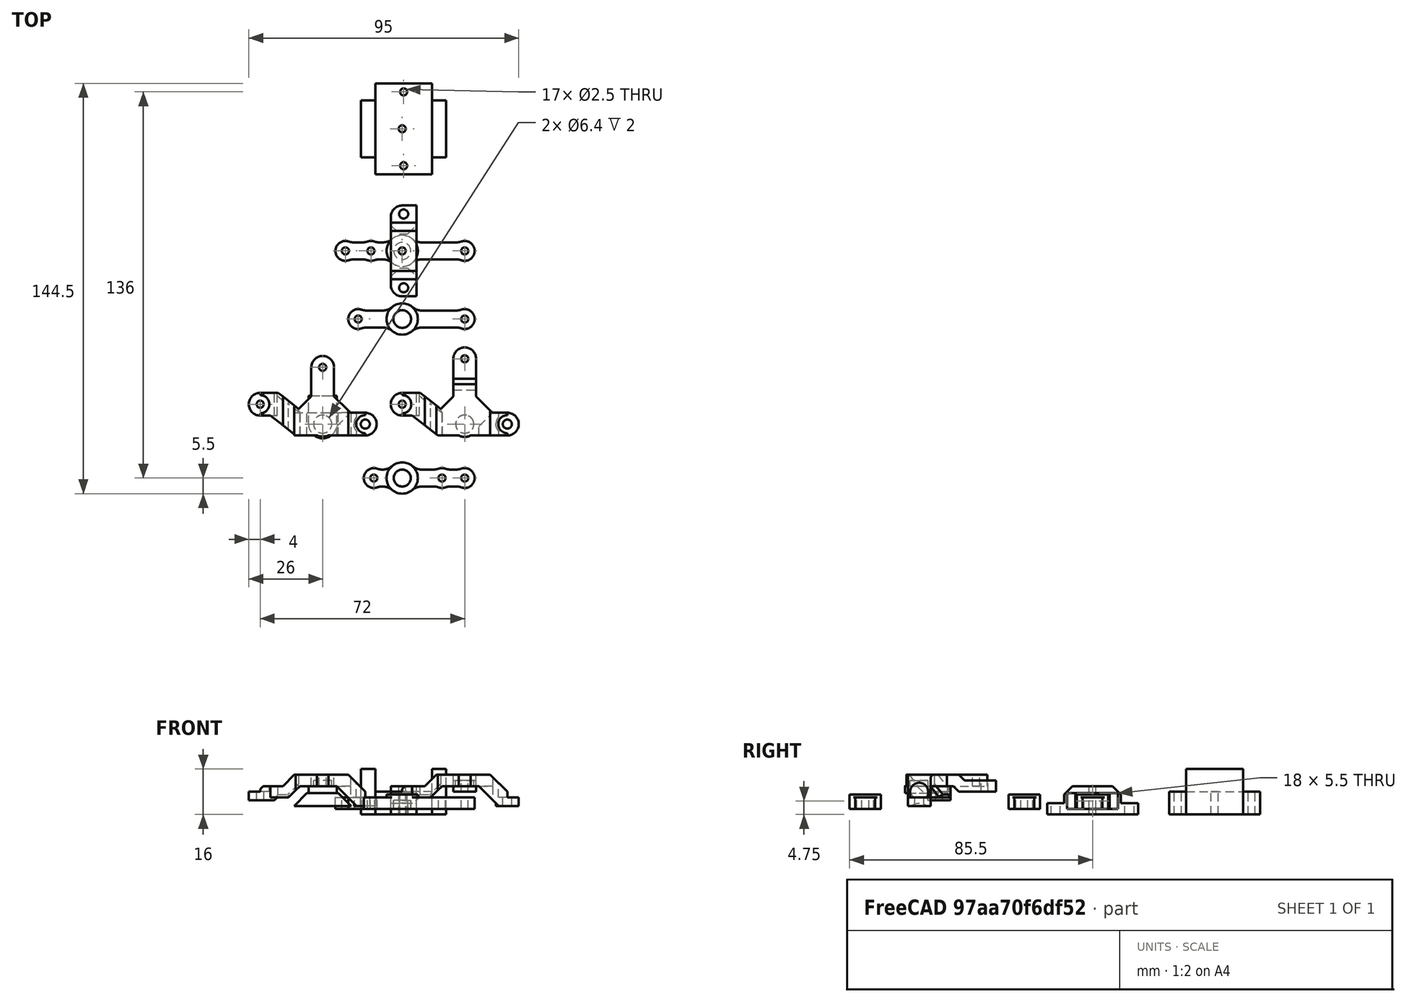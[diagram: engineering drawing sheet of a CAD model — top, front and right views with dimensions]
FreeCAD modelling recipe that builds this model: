
FCSTD DOCUMENT  (FreeCAD 0.20R)
Label: steering-arms-04
License: CC-BY 3.0
LicenseURL: http://creativecommons.org/licenses/by/3.0/
objects: Part::Cylinder×49, Part::MultiFuse×31, Part::Box×30, Part::Cut×30, Part::Chamfer×13, Part::Fillet×5, App::DocumentObjectGroup×2, Part::Mirroring×1
note: 159 computed .brp shape members not serialized (recipe doc carries the construction recipe); baked Part::Feature solids carry a one-line shape summary decoded from their .brp

FEATURE [Part::Cylinder] Cylinder011
  Angle = 360
  AttacherType = Attacher::AttachEngine3D
  FirstAngle = 0
  Height = 2.5
  Placement = pos=(-15,0,5.5) rot=(0,0,1;0rad)
  Radius = 5
  SecondAngle = 0
FEATURE [Part::Box] Box014  label="Cube014"
  AttacherType = Attacher::AttachEngine3D
  Height = 2.5
  Length = 10
  Placement = pos=(-20,0,5.5) rot=(0,0,1;0rad)
  Width = 10
FEATURE [Part::MultiFuse] Fusion006
  Refine = true
  Shapes = -> [Cylinder011,Box014]
FEATURE [Part::Box] Box015  label="Cube015"
  AttacherType = Attacher::AttachEngine3D
  Height = 4.5
  Length = 20
  Placement = pos=(-25,-4,1) rot=(0,0,1;0rad)
  Width = 8
FEATURE [Part::Chamfer] Chamfer001
  Base = -> Box015
  Edges = 2 edges r=4.49: [Edge2,Edge6]
FEATURE [Part::MultiFuse] Fusion008  label="axle"
  Refine = true
  Shapes = -> [Chamfer001,Fusion006]
FEATURE [Part::Cylinder] Cylinder016
  Angle = 360
  AttacherType = Attacher::AttachEngine3D
  FirstAngle = 0
  Height = 3
  Placement = pos=(0,0,1) rot=(0,0,1;0rad)
  Radius = 4
  SecondAngle = 0
FEATURE [Part::Cylinder] Cylinder017
  Angle = 360
  AttacherType = Attacher::AttachEngine3D
  FirstAngle = 0
  Height = 3
  Placement = pos=(-37,7,3) rot=(0,0,1;0rad)
  Radius = 4
  SecondAngle = 0
FEATURE [Part::Cylinder] Cylinder018
  Angle = 360
  AttacherType = Attacher::AttachEngine3D
  FirstAngle = 0
  Height = 4
  Placement = pos=(-15,0,8) rot=(0,0,1;0rad)
  Radius = 4.5
  SecondAngle = 0
FEATURE [Part::Box] Box021  label="Cube021"
  AttacherType = Attacher::AttachEngine3D
  Height = 4
  Length = 8
  Placement = pos=(-19,0,8) rot=(0,0,1;0rad)
  Width = 27
FEATURE [Part::Cylinder] Cylinder019
  Angle = 360
  AttacherType = Attacher::AttachEngine3D
  FirstAngle = 0
  Height = 4
  Placement = pos=(-15,27,8) rot=(0,0,1;0rad)
  Radius = 4
  SecondAngle = 0
FEATURE [Part::Cylinder] Cylinder020
  Angle = 360
  AttacherType = Attacher::AttachEngine3D
  FirstAngle = 0
  Height = 2
  Placement = pos=(-15,0,8) rot=(0,0,1;0rad)
  Radius = 3.2
  SecondAngle = 0
FEATURE [Part::Box] Box022  label="Cube022"
  AttacherType = Attacher::AttachEngine3D
  Height = 4
  Length = 11
  Placement = pos=(-15,-4,8) rot=(0,0,1;0rad)
  Width = 8
FEATURE [Part::Box] Box023  label="Cube023"
  AttacherType = Attacher::AttachEngine3D
  Height = 4
  Length = 6
  Placement = pos=(-37,3,8) rot=(0,0,1;0rad)
  Width = 8
FEATURE [Part::Box] Box024  label="Cube024"
  AttacherType = Attacher::AttachEngine3D
  Height = 4
  Length = 15
  Placement = pos=(-36,5,8) rot=(0,0,-1;0.663225rad)
  Width = 8
FEATURE [Part::Box] Box025  label="Cube025"
  AttacherType = Attacher::AttachEngine3D
  Height = 4
  Length = 9
  Placement = pos=(-24,-4,8) rot=(0,0,1;0rad)
  Width = 8
FEATURE [Part::Box] Box026  label="Cube026"
  AttacherType = Attacher::AttachEngine3D
  Height = 4
  Length = 10
  Placement = pos=(-30,-14,8) rot=(0,0,1;0rad)
  Width = 10
FEATURE [Part::Box] Box027  label="Cube027"
  AttacherType = Attacher::AttachEngine3D
  Height = 4
  Length = 10
  Placement = pos=(-35,11,8) rot=(0,0,1;0rad)
  Width = 10
FEATURE [Part::MultiFuse] Fusion016
  Refine = true
  Shapes = -> [Box026,Box027]
FEATURE [Part::MultiFuse] Fusion017
  Refine = true
  Shapes = -> [Box023,Box024,Box025]
FEATURE [Part::Cut] Cut012
  Base = -> Fusion017
  Refine = true
  Tool = -> Fusion016
FEATURE [Part::Cylinder] Cylinder021
  Angle = 360
  AttacherType = Attacher::AttachEngine3D
  FirstAngle = 0
  Height = 10
  Radius = 1.6
  SecondAngle = 0
FEATURE [Part::Cylinder] Cylinder022
  Angle = 360
  AttacherType = Attacher::AttachEngine3D
  FirstAngle = 0
  Height = 10
  Placement = pos=(-37,7,2) rot=(0,0,1;0rad)
  Radius = 1.6
  SecondAngle = 0
FEATURE [Part::Box] Box028  label="Cube028"
  AttacherType = Attacher::AttachEngine3D
  Height = 4
  Length = 14
  Placement = pos=(-15,-6,8) rot=(0,0,1;0.785398rad)
  Width = 14
FEATURE [Part::Box] Box029  label="Cube029"
  AttacherType = Attacher::AttachEngine3D
  Height = 4
  Length = 10
  Placement = pos=(-20,-14,8) rot=(0,0,1;0rad)
  Width = 10
FEATURE [Part::Cut] Cut013
  Base = -> Box028
  Refine = true
  Tool = -> Box029
FEATURE [Part::MultiFuse] Fusion018
  Refine = true
  Shapes = -> [Box022,Box021,Cut013,Cut012,Cylinder019,Cylinder018]
FEATURE [Part::Cut] Cut014
  Base = -> Fusion018
  Refine = true
  Tool = -> Cylinder020
FEATURE [Part::Box] Box032  label="Cube032"
  AttacherType = Attacher::AttachEngine3D
  Height = 11
  Length = 10
  Placement = pos=(-10,-4,1) rot=(0,0,1;0rad)
  Width = 8
FEATURE [Part::Chamfer] Chamfer012
  Base = -> Box032
  Edges = 1 edges r=7: [Edge4]
FEATURE [Part::Chamfer] Chamfer013
  Base = -> Chamfer012
  Edges = 1 edges r=6: [Edge12]
FEATURE [Part::Chamfer] Chamfer014
  Base = -> Cut014
  Edges = 1 edges r=2: [Edge2]
FEATURE [Part::MultiFuse] Fusion020
  Refine = true
  Shapes = -> [Chamfer014,Chamfer013]
FEATURE [Part::Cylinder] Cylinder024
  Angle = 360
  AttacherType = Attacher::AttachEngine3D
  FirstAngle = 0
  Height = 10
  Placement = pos=(0,0,4) rot=(0,0,1;0rad)
  Radius = 3.2
  SecondAngle = 0
FEATURE [Part::Cut] Cut015
  Base = -> Fusion020
  Refine = true
  Tool = -> Cylinder024
FEATURE [Part::Box] Box033  label="Cube033"
  AttacherType = Attacher::AttachEngine3D
  Height = 8
  Length = 10
  Placement = pos=(-10.2,-1,0) rot=(0,0,1;0.785398rad)
  Width = 10
FEATURE [Part::Cut] Cut016
  Base = -> Cut015
  Refine = true
  Tool = -> Box033
FEATURE [Part::MultiFuse] Fusion022
  Refine = true
  Shapes = -> [Cylinder016,Cut016]
FEATURE [Part::Cylinder] Cylinder025
  Angle = 360
  AttacherType = Attacher::AttachEngine3D
  FirstAngle = 0
  Height = 10
  Placement = pos=(-15,27,4) rot=(0,0,1;0rad)
  Radius = 1.6
  SecondAngle = 0
FEATURE [Part::MultiFuse] Fusion023
  Refine = true
  Shapes = -> [Cylinder021,Cylinder025]
FEATURE [Part::Cut] Cut017
  Base = -> Fusion022
  Refine = true
  Tool = -> Fusion023
FEATURE [Part::MultiFuse] Fusion024
  Refine = true
  Shapes = -> [Box026,Box027]
FEATURE [Part::MultiFuse] Fusion025
  Refine = true
  Shapes = -> [Box023,Box024,Box025]
FEATURE [Part::Cut] Cut018
  Base = -> Fusion025
  Placement = pos=(0,0,-4) rot=(0,0,1;0rad)
  Refine = true
  Tool = -> Fusion024
FEATURE [Part::Box] Box034  label="Cube034"
  AttacherType = Attacher::AttachEngine3D
  Height = 10
  Length = 10
  Placement = pos=(-23,-4,0) rot=(0,0,1;0rad)
  Width = 11
FEATURE [Part::Cut] Cut019
  Base = -> Cut018
  Refine = true
  Tool = -> Box034
FEATURE [Part::Chamfer] Chamfer015
  Base = -> Cut019
  Edges = 1 edges r=3.99: [Edge20]
FEATURE [Part::Box] Box035  label="Cube035"
  AttacherType = Attacher::AttachEngine3D
  Height = 10
  Length = 10
  Placement = pos=(-39,-2,8) rot=(0,0,1;0rad)
  Width = 15
FEATURE [Part::Cut] Cut020
  Base = -> Cut017
  Refine = true
  Tool = -> Box035
FEATURE [Part::Chamfer] Chamfer016
  Base = -> Cut020
  Edges = 1 edges r=3.99: [Edge32]
FEATURE [Part::MultiFuse] Fusion026
  Refine = true
  Shapes = -> [Chamfer015,Chamfer016]
FEATURE [Part::MultiFuse] Fusion027
  Refine = true
  Shapes = -> [Cylinder017,Fusion026]
FEATURE [Part::Cylinder] Cylinder026
  Angle = 360
  AttacherType = Attacher::AttachEngine3D
  FirstAngle = 0
  Height = 10
  Placement = pos=(-37,7,6) rot=(0,0,1;0rad)
  Radius = 3.2
  SecondAngle = 0
FEATURE [Part::Chamfer] Chamfer017
  Base = -> Fusion027
  Edges = 1 edges r=1: [Edge20]
FEATURE [Part::Cut] Cut021
  Base = -> Chamfer017
  Refine = true
  Tool = -> Cylinder026
FEATURE [Part::Box] Box036  label="Cube036"
  AttacherType = Attacher::AttachEngine3D
  Height = 1
  Length = 6
  Placement = pos=(-37,3,3) rot=(0,0,1;0rad)
  Width = 8
FEATURE [Part::MultiFuse] Fusion028
  Refine = true
  Shapes = -> [Cut021,Box036]
FEATURE [Part::Chamfer] Chamfer018
  Base = -> Fusion028
  Edges = 1 edges r=0.99: [Edge51]
FEATURE [Part::Cut] Cut022
  Base = -> Chamfer018
  Refine = true
  Tool = -> Cylinder022
FEATURE [Part::Chamfer] Chamfer019
  Base = -> Cut022
  Edges = 2 edges r=1: [Edge17,Edge50]
FEATURE [Part::Box] Box037  label="Cube037"
  AttacherType = Attacher::AttachEngine3D
  Height = 10
  Length = 10
  Placement = pos=(-19,23,3) rot=(0,0,1;0rad)
  Width = 10
FEATURE [Part::Cut] Cut023
  Base = -> Chamfer019
  Refine = true
  Tool = -> Box037
FEATURE [Part::Cylinder] Cylinder027
  Angle = 360
  AttacherType = Attacher::AttachEngine3D
  FirstAngle = 0
  Height = 4
  Placement = pos=(-15,23,8) rot=(0,0,1;0rad)
  Radius = 4
  SecondAngle = 0
FEATURE [Part::MultiFuse] Fusion029
  Refine = true
  Shapes = -> [Cut023,Cylinder027]
FEATURE [Part::Cylinder] Cylinder028
  Angle = 360
  AttacherType = Attacher::AttachEngine3D
  FirstAngle = 0
  Height = 4
  Placement = pos=(-15,23,8) rot=(0,0,1;0rad)
  Radius = 1.6
  SecondAngle = 0
FEATURE [Part::Cut] Cut024
  Base = -> Fusion029
  Placement = pos=(50,0,0) rot=(0,0,1;0rad)
  Refine = true
  Tool = -> Cylinder028
FEATURE [Part::Cylinder] Cylinder029
  Angle = 360
  AttacherType = Attacher::AttachEngine3D
  FirstAngle = 0
  Height = 5
  Placement = pos=(13,0,0) rot=(0,0,1;0rad)
  Radius = 5.5
  SecondAngle = 0
FEATURE [Part::Cylinder] Cylinder030
  Angle = 360
  AttacherType = Attacher::AttachEngine3D
  FirstAngle = 0
  Height = 4
  Placement = pos=(35,0,0) rot=(0,0,1;0rad)
  Radius = 3.5
  SecondAngle = 0
FEATURE [Part::Box] Box038
  AttacherType = Attacher::AttachEngine3D
  Height = 4
  Length = 33
  Placement = pos=(2,-3,0) rot=(0,0,1;0rad)
  Width = 6
FEATURE [Part::Cylinder] Cylinder031
  Angle = 360
  AttacherType = Attacher::AttachEngine3D
  FirstAngle = 0
  Height = 4
  Placement = pos=(2,0,0) rot=(0,0,1;0rad)
  Radius = 3.5
  SecondAngle = 0
FEATURE [Part::MultiFuse] Fusion030
  Refine = true
  Shapes = -> [Cylinder029,Box038,Cylinder031,Cylinder030]
FEATURE [Part::Cylinder] Cylinder032
  Angle = 360
  AttacherType = Attacher::AttachEngine3D
  FirstAngle = 0
  Height = 5
  Placement = pos=(13,0,0) rot=(0,0,1;0rad)
  Radius = 3
  SecondAngle = 0
FEATURE [Part::Cylinder] Cylinder033
  Angle = 360
  AttacherType = Attacher::AttachEngine3D
  FirstAngle = 0
  Height = 4
  Placement = pos=(2,0,0) rot=(0,0,1;0rad)
  Radius = 1.25
  SecondAngle = 0
FEATURE [Part::Cylinder] Cylinder034
  Angle = 360
  AttacherType = Attacher::AttachEngine3D
  FirstAngle = 0
  Height = 4
  Placement = pos=(35,0,0) rot=(0,0,1;0rad)
  Radius = 1.25
  SecondAngle = 0
FEATURE [Part::MultiFuse] Fusion031
  Refine = true
  Shapes = -> [Cylinder032,Cylinder033,Cylinder034]
FEATURE [Part::Cut] Cut025
  Base = -> Fusion030
  Refine = true
  Tool = -> Fusion031
FEATURE [Part::Cylinder] Cylinder035
  Angle = 360
  AttacherType = Attacher::AttachEngine3D
  FirstAngle = 0
  Height = 5
  Placement = pos=(13,0,0) rot=(0,0,1;0rad)
  Radius = 5.5
  SecondAngle = 0
FEATURE [Part::Cylinder] Cylinder036
  Angle = 360
  AttacherType = Attacher::AttachEngine3D
  FirstAngle = 0
  Height = 4
  Placement = pos=(35,0,0) rot=(0,0,1;0rad)
  Radius = 3.5
  SecondAngle = 0
FEATURE [Part::Box] Box039
  AttacherType = Attacher::AttachEngine3D
  Height = 4
  Length = 38
  Placement = pos=(-3,-3,0) rot=(0,0,1;0rad)
  Width = 6
FEATURE [Part::Cylinder] Cylinder037
  Angle = 360
  AttacherType = Attacher::AttachEngine3D
  FirstAngle = 0
  Height = 4
  Placement = pos=(-2.5,0,0) rot=(0,0,1;0rad)
  Radius = 3.5
  SecondAngle = 0
FEATURE [Part::MultiFuse] Fusion032
  Refine = true
  Shapes = -> [Cylinder035,Box039,Cylinder037,Cylinder036]
FEATURE [Part::Cylinder] Cylinder038
  Angle = 360
  AttacherType = Attacher::AttachEngine3D
  FirstAngle = 0
  Height = 5
  Placement = pos=(13,0,0) rot=(0,0,1;0rad)
  Radius = 3.1
  SecondAngle = 0
FEATURE [Part::Cylinder] Cylinder039
  Angle = 360
  AttacherType = Attacher::AttachEngine3D
  FirstAngle = 0
  Height = 4
  Placement = pos=(-2.5,0,0) rot=(0,0,1;0rad)
  Radius = 1.25
  SecondAngle = 0
FEATURE [Part::Cylinder] Cylinder040
  Angle = 360
  AttacherType = Attacher::AttachEngine3D
  FirstAngle = 0
  Height = 4
  Placement = pos=(35,0,0) rot=(0,0,1;0rad)
  Radius = 1.25
  SecondAngle = 0
FEATURE [Part::MultiFuse] Fusion033
  Refine = true
  Shapes = -> [Cylinder038,Cylinder039,Cylinder040]
FEATURE [Part::Cut] Cut026
  Base = -> Fusion032
  Placement = pos=(0,25,0) rot=(0,0,1;0rad)
  Refine = true
  Tool = -> Fusion033
FEATURE [Part::Cylinder] Cylinder041
  Angle = 360
  AttacherType = Attacher::AttachEngine3D
  FirstAngle = 0
  Height = 4
  Placement = pos=(-7,0,0) rot=(0,0,1;0rad)
  Radius = 3.5
  SecondAngle = 0
FEATURE [Part::Cylinder] Cylinder042
  Angle = 360
  AttacherType = Attacher::AttachEngine3D
  FirstAngle = 0
  Height = 4
  Placement = pos=(-7,0,0) rot=(0,0,1;0rad)
  Radius = 1.25
  SecondAngle = 0
FEATURE [Part::Cylinder] Cylinder043
  Angle = 360
  AttacherType = Attacher::AttachEngine3D
  FirstAngle = 0
  Height = 5
  Placement = pos=(13,0,0) rot=(0,0,1;0rad)
  Radius = 5.5
  SecondAngle = 0
FEATURE [Part::Cylinder] Cylinder044
  Angle = 360
  AttacherType = Attacher::AttachEngine3D
  FirstAngle = 0
  Height = 4
  Placement = pos=(35,0,0) rot=(0,0,1;0rad)
  Radius = 3.5
  SecondAngle = 0
FEATURE [Part::Box] Box040
  AttacherType = Attacher::AttachEngine3D
  Height = 4
  Length = 32
  Placement = pos=(3,-3,0) rot=(0,0,1;0rad)
  Width = 6
FEATURE [Part::Cylinder] Cylinder045
  Angle = 360
  AttacherType = Attacher::AttachEngine3D
  FirstAngle = 0
  Height = 4
  Placement = pos=(3,0,0) rot=(0,0,1;0rad)
  Radius = 3.5
  SecondAngle = 0
FEATURE [Part::MultiFuse] Fusion034
  Refine = true
  Shapes = -> [Cylinder043,Box040,Cylinder045,Cylinder044]
FEATURE [Part::Cylinder] Cylinder046
  Angle = 360
  AttacherType = Attacher::AttachEngine3D
  FirstAngle = 0
  Height = 5
  Placement = pos=(13,0,0) rot=(0,0,1;0rad)
  Radius = 3
  SecondAngle = 0
FEATURE [Part::Cylinder] Cylinder047
  Angle = 360
  AttacherType = Attacher::AttachEngine3D
  FirstAngle = 0
  Height = 4
  Placement = pos=(3,0,0) rot=(0,0,1;0rad)
  Radius = 1.25
  SecondAngle = 0
FEATURE [Part::Cylinder] Cylinder048
  Angle = 360
  AttacherType = Attacher::AttachEngine3D
  FirstAngle = 0
  Height = 4
  Placement = pos=(35,0,0) rot=(0,0,1;0rad)
  Radius = 1.25
  SecondAngle = 0
FEATURE [Part::MultiFuse] Fusion035
  Refine = true
  Shapes = -> [Cylinder046,Cylinder047,Cylinder048]
FEATURE [Part::Cut] Cut027
  Base = -> Fusion034
  Refine = true
  Tool = -> Fusion035
FEATURE [Part::Cylinder] Cylinder049
  Angle = 360
  AttacherType = Attacher::AttachEngine3D
  FirstAngle = 0
  Height = 4
  Placement = pos=(27,0,0) rot=(0,0,1;0rad)
  Radius = 3.5
  SecondAngle = 0
FEATURE [Part::Cylinder] Cylinder050
  Angle = 360
  AttacherType = Attacher::AttachEngine3D
  FirstAngle = 0
  Height = 4
  Placement = pos=(27,0,0) rot=(0,0,1;0rad)
  Radius = 1.25
  SecondAngle = 0
FEATURE [Part::MultiFuse] Fusion036
  Refine = true
  Shapes = -> [Cylinder049,Cut027]
FEATURE [Part::Cut] Cut028
  Base = -> Fusion036
  Placement = pos=(0,-19,0) rot=(0,0,1;0rad)
  Refine = true
  Tool = -> Cylinder050
FEATURE [Part::MultiFuse] Fusion037
  Refine = true
  Shapes = -> [Cylinder041,Cut025]
FEATURE [Part::Cut] Cut029
  Base = -> Fusion037
  Refine = true
  Tool = -> Cylinder042
FEATURE [Part::Fillet] Fillet
  Base = -> Cut028
  Edges = 12 edges r=5: [Edge2,Edge4,Edge6,Edge11,Edge28,Edge32,Edge33,Edge45,Edge46,Edge47,Edge49,Edge50]
FEATURE [Part::Box] Box041  label="Cube038"
  AttacherType = Attacher::AttachEngine3D
  Height = 10
  Length = 9
  Placement = pos=(7,-10,-2) rot=(0,0,1;0rad)
  Width = 20
FEATURE [Part::Box] Box042  label="Cube039"
  AttacherType = Attacher::AttachEngine3D
  Height = 5.5
  Length = 12
  Placement = pos=(7,-6,0) rot=(0,0,1;0rad)
  Width = 12
FEATURE [Part::Cut] Cut030
  Base = -> Box041
  Refine = true
  Tool = -> Box042
FEATURE [Part::Chamfer] Chamfer
  Base = -> Cut030
  Edges = 4 edges r=3: [Edge5,Edge7,Edge18,Edge22]
  Placement = pos=(1,0,0) rot=(0,0,1;0rad)
FEATURE [Part::Chamfer] Chamfer020
  Base = -> Chamfer
  Edges = 2 edges r=3: [Edge35,Edge36]
FEATURE [Part::Cylinder] Cylinder051
  Angle = 360
  AttacherType = Attacher::AttachEngine3D
  FirstAngle = 0
  Height = 12
  Placement = pos=(12,0,-2) rot=(0,0,1;0rad)
  Radius = 1.25
  SecondAngle = 0
FEATURE [Part::Cut] Cut031
  Base = -> Chamfer020
  Placement = pos=(1,0,0) rot=(0,0,1;0rad)
  Refine = true
  Tool = -> Cylinder051
FEATURE [App::DocumentObjectGroup] Group  label="Deleted"
  Group = -> [Fillet]
FEATURE [Part::Box] Box043  label="Cube002"
  AttacherType = Attacher::AttachEngine3D
  Height = 4
  Length = 9
  Placement = pos=(9,10,-2) rot=(0,0,1;0rad)
  Width = 6
FEATURE [Part::Cylinder] Cylinder052
  Angle = 360
  AttacherType = Attacher::AttachEngine3D
  FirstAngle = 0
  Height = 10
  Placement = pos=(13.5,13,-3) rot=(0,0,1;0rad)
  Radius = 1.6
  SecondAngle = 0
FEATURE [Part::Cut] Cut032
  Base = -> Box043
  Refine = true
  Tool = -> Cylinder052
FEATURE [Part::Fillet] Fillet001
  Base = -> Cut032
  Edges = 1 edges r=4: [Edge3]
FEATURE [Part::Cut] Cut033
  Base = -> Box043
  Refine = true
  Tool = -> Cylinder052
FEATURE [Part::Fillet] Fillet002
  Base = -> Cut033
  Edges = 1 edges r=4: [Edge3]
FEATURE [Part::Mirroring] Part__Mirroring  label="Fillet004 (Mirror #1)"
  Base = (0,0,0)
  Normal = (0,1,0)
  Source = -> Fillet001
FEATURE [Part::Box] Box044
  AttacherType = Attacher::AttachEngine3D
  Height = 4
  Length = 6
  Placement = pos=(-5.5,-3,0) rot=(0,0,1;0rad)
  Width = 6
FEATURE [Part::MultiFuse] Fusion039
  Refine = true
  Shapes = -> [Cut029,Box044]
FEATURE [Part::Cylinder] Cylinder053
  Angle = 360
  AttacherType = Attacher::AttachEngine3D
  FirstAngle = 0
  Height = 10
  Placement = pos=(13,0,-3) rot=(0,0,1;0rad)
  Radius = 1.25
  SecondAngle = 0
FEATURE [Part::Cylinder] Cylinder054
  Angle = 360
  AttacherType = Attacher::AttachEngine3D
  FirstAngle = 0
  Height = 10
  Placement = pos=(13.5,-13,-3) rot=(0,0,1;0rad)
  Radius = 1.25
  SecondAngle = 0
FEATURE [Part::Cylinder] Cylinder055
  Angle = 360
  AttacherType = Attacher::AttachEngine3D
  FirstAngle = 0
  Height = 10
  Placement = pos=(13.5,13,-3) rot=(0,0,1;0rad)
  Radius = 1.25
  SecondAngle = 0
FEATURE [Part::Box] Box045
  AttacherType = Attacher::AttachEngine3D
  Height = 16
  Length = 20
  Placement = pos=(-10,14.5,0) rot=(0,0,1;0rad)
  Width = 5
FEATURE [Part::Box] Box046
  AttacherType = Attacher::AttachEngine3D
  Height = 16
  Length = 20
  Placement = pos=(-10,39.5,0) rot=(0,0,1;0rad)
  Width = 5
FEATURE [Part::Box] Box047
  AttacherType = Attacher::AttachEngine3D
  Height = 8
  Length = 32
  Placement = pos=(-16,19.5,0) rot=(0,0,1;0rad)
  Width = 20
FEATURE [Part::MultiFuse] Fusion040
  Placement = pos=(43,0,-2) rot=(0,0,1;1.5708rad)
  Refine = true
  Shapes = -> [Box045,Box047,Box046]
FEATURE [Part::MultiFuse] Fusion041
  Refine = true
  Shapes = -> [Cylinder053,Cylinder054,Cylinder055]
FEATURE [Part::Cut] Cut034  label="steering-lever-holder-HOLES-TOOL"
  Base = -> Fusion040
  Placement = pos=(0,104,0) rot=(0,0,1;0rad)
  Refine = true
  Tool = -> Fusion041
FEATURE [Part::Fillet] Fillet003  label="steering-lever-front"
  Base = -> Fusion039
  Edges = 12 edges r=5: [Edge6,Edge8,Edge10,Edge13,Edge16,Edge18,Edge22,Edge25,Edge30,Edge34,Edge35,Edge38]
  Placement = pos=(0,61,0) rot=(0,0,1;0rad)
FEATURE [Part::Fillet] Fillet004  label="steering-lever-rear"
  Base = -> Cut026
  Edges = 8 edges r=5: [Edge5,Edge7,Edge9,Edge11,Edge21,Edge31,Edge35,Edge36]
  Placement = pos=(0,12,0) rot=(0,0,1;0rad)
FEATURE [Part::Cylinder] Cylinder
  Angle = 360
  AttacherType = Attacher::AttachEngine3D
  FirstAngle = 0
  Height = 4
  Placement = pos=(-15,23,8) rot=(0,0,1;0rad)
  Radius = 1.6
  SecondAngle = 0
FEATURE [Part::MultiFuse] Fusion
  Refine = true
  Shapes = -> [Cut023,Cylinder027]
FEATURE [Part::Cut] Cut
  Base = -> Fusion
  Refine = true
  Tool = -> Cylinder
FEATURE [Part::Cylinder] Cylinder056
  Angle = 360
  AttacherType = Attacher::AttachEngine3D
  FirstAngle = 0
  Height = 4
  Placement = pos=(-15,20,8) rot=(0,0,1;0rad)
  Radius = 4
  SecondAngle = 0
FEATURE [Part::Box] Box  label="Cube"
  AttacherType = Attacher::AttachEngine3D
  Height = 10
  Length = 10
  Placement = pos=(-20,20,2) rot=(0,0,1;0rad)
  Width = 10
FEATURE [Part::Cut] Cut035
  Base = -> Cut
  Refine = true
  Tool = -> Box
FEATURE [Part::Cylinder] Cylinder057
  Angle = 360
  AttacherType = Attacher::AttachEngine3D
  FirstAngle = 0
  Height = 4
  Placement = pos=(-15,20,8) rot=(0,0,1;0rad)
  Radius = 1.25
  SecondAngle = 0
FEATURE [Part::MultiFuse] Fusion042
  Refine = true
  Shapes = -> [Cut035,Cylinder056]
FEATURE [Part::Cut] Cut036
  Base = -> Fusion042
  Refine = true
  Tool = -> Cylinder057
FEATURE [Part::Cylinder] Cylinder058
  Angle = 360
  AttacherType = Attacher::AttachEngine3D
  FirstAngle = 0
  Height = 3
  Placement = pos=(-37,7,3) rot=(0,0,1;0rad)
  Radius = 2
  SecondAngle = 0
FEATURE [Part::Cylinder] Cylinder060
  Angle = 360
  AttacherType = Attacher::AttachEngine3D
  FirstAngle = 0
  Height = 3
  Placement = pos=(-37,7,3) rot=(0,0,1;0rad)
  Radius = 1.25
  SecondAngle = 0
FEATURE [Part::MultiFuse] Fusion043
  Refine = true
  Shapes = -> [Cylinder058,Cut036]
FEATURE [Part::Cut] Cut037  label="steering-arm-rear"
  Base = -> Fusion043
  Refine = true
  Tool = -> Cylinder060
FEATURE [Part::Box] Box048  label="Cube040"
  AttacherType = Attacher::AttachEngine3D
  Height = 2
  Length = 8
  Placement = pos=(31,12,6) rot=(0,0,1;0rad)
  Width = 11
FEATURE [Part::Box] Box049  label="Cube041"
  AttacherType = Attacher::AttachEngine3D
  Height = 2
  Length = 8
  Placement = pos=(31,14,10) rot=(0,0,1;0rad)
  Width = 13
FEATURE [Part::Cut] Cut038
  Base = -> Cut024
  Refine = true
  Tool = -> Box049
FEATURE [Part::Cylinder] Cylinder061
  Angle = 360
  AttacherType = Attacher::AttachEngine3D
  FirstAngle = 0
  Height = 4
  Placement = pos=(35,23,6) rot=(0,0,1;0rad)
  Radius = 4
  SecondAngle = 0
FEATURE [Part::Cylinder] Cylinder062
  Angle = 360
  AttacherType = Attacher::AttachEngine3D
  FirstAngle = 0
  Height = 4
  Placement = pos=(35,23,6) rot=(0,0,1;0rad)
  Radius = 1.25
  SecondAngle = 0
FEATURE [Part::MultiFuse] Fusion044
  Refine = true
  Shapes = -> [Cut038,Box048,Cylinder061]
FEATURE [Part::Cut] Cut039
  Base = -> Fusion044
  Refine = true
  Tool = -> Cylinder062
FEATURE [Part::Chamfer] Chamfer021
  Base = -> Cut039
  Edges = 1 edges r=1.99: [Edge1]
FEATURE [Part::Chamfer] Chamfer022
  Base = -> Chamfer021
  Edges = 1 edges r=1.99: [Edge51]
FEATURE [Part::Cylinder] Cylinder063
  Angle = 360
  AttacherType = Attacher::AttachEngine3D
  FirstAngle = 0
  Height = 3
  Placement = pos=(13,7,3) rot=(0,0,1;0rad)
  Radius = 2
  SecondAngle = 0
FEATURE [Part::Cylinder] Cylinder064
  Angle = 360
  AttacherType = Attacher::AttachEngine3D
  FirstAngle = 0
  Height = 3
  Placement = pos=(13,7,3) rot=(0,0,1;0rad)
  Radius = 1.25
  SecondAngle = 0
FEATURE [Part::MultiFuse] Fusion045
  Refine = true
  Shapes = -> [Chamfer022,Cylinder063]
FEATURE [Part::Cut] Cut040  label="steering-arm-front"
  Base = -> Fusion045
  Refine = true
  Tool = -> Cylinder064
FEATURE [Part::MultiFuse] Fusion046  label="steering-lever-holder-front"
  Placement = pos=(0,61,0) rot=(0,0,1;0rad)
  Refine = true
  Shapes = -> [Cut031,Fillet002,Part__Mirroring]
FEATURE [App::DocumentObjectGroup] Group001  label="Tools"
  Group = -> [Cut034]
